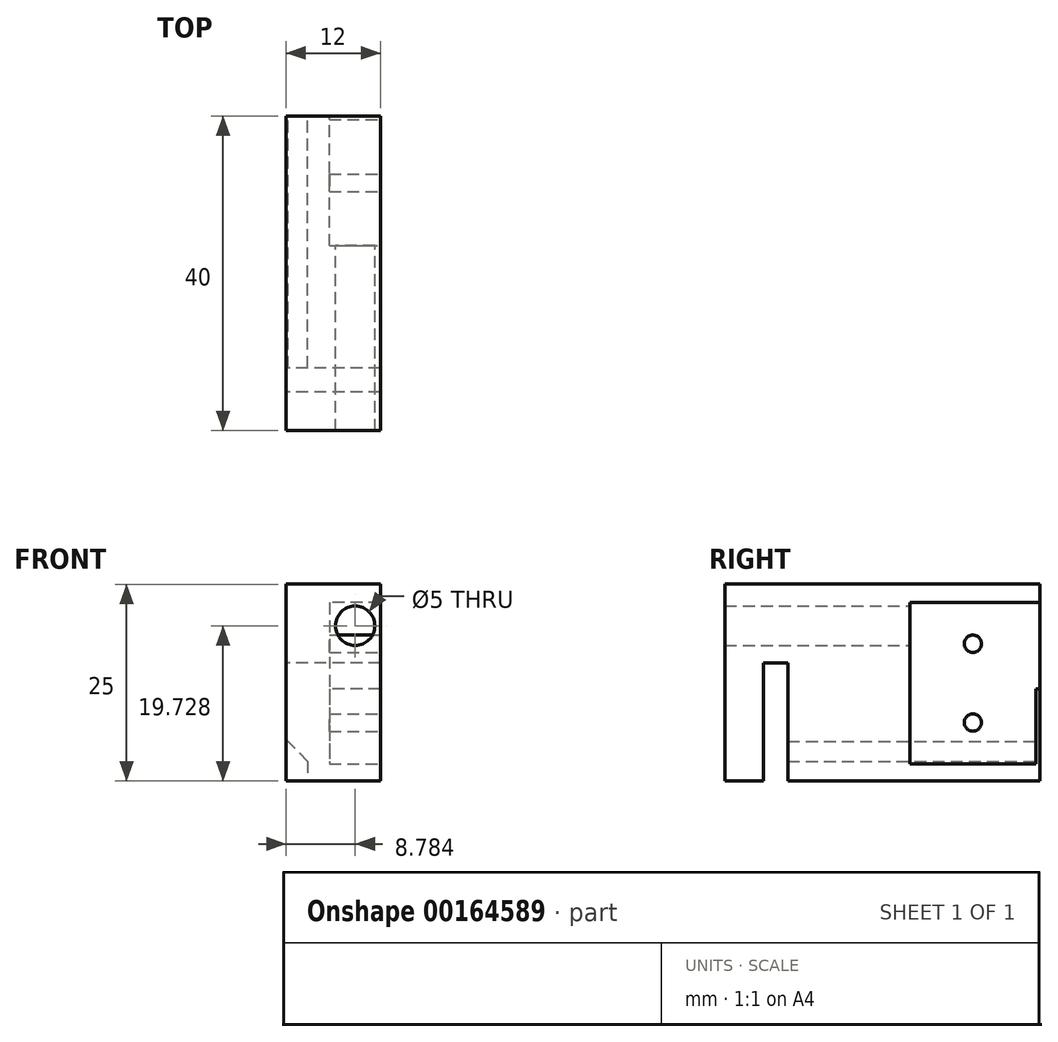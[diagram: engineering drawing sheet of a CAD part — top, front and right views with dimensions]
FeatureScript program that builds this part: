
annotation { "Feature Type Name" : "Feature", "Feature Type Description" : "" }
export const myFeature = defineFeature(function(context is Context, id is Id, definition is map)
    precondition{}
    {
        {
            var Q0;
            Q0=qCreatedBy(makeId("Right.planeOp"),FACE);
            var sketch = newSketch(context, id + "F0", { "sketchPlane" : qUnion([Q0])});
            skLineSegment(sketch, "E0.bottom", {"start": v(-4.9, -0.08) * mm, "end": v(35.1, -0.08) * mm});
            skLineSegment(sketch, "E0.top", {"start": v(-4.9, -25.08) * mm, "end": v(35.1, -25.08) * mm});
            skLineSegment(sketch, "E0.left", {"start": v(-4.9, -0.08) * mm, "end": v(-4.9, -25.08) * mm});
            skLineSegment(sketch, "E0.right", {"start": v(35.1, -0.08) * mm, "end": v(35.1, -25.08) * mm});
            skLineSegment(sketch, "E1.bottom", {"start": v(0, -25.08) * mm, "end": v(3.1, -25.08) * mm});
            skLineSegment(sketch, "E1.top", {"start": v(0, -10.08) * mm, "end": v(3.1, -10.08) * mm});
            skLineSegment(sketch, "E1.left", {"start": v(0, -25.08) * mm, "end": v(0, -10.08) * mm});
            skLineSegment(sketch, "E1.right", {"start": v(3.1, -25.08) * mm, "end": v(3.1, -10.08) * mm});
            skSolve(sketch);
        }
        {
            var Q0;
            Q0=makeQuery(id+"F0.imprint","IMPRINT",FACE,{"disambiguationData":[TD([[makeQuery(id+"F0.imprint","IMPRINT",EDGE,{"derivedFrom":sQuery(id+"F0.wireOp",EDGE,"E0.bottom")}),-1.0]])]});
            extrude(context, id + "F1", {"entities" : qUnion([Q0]), "depth" : 12 * mm});
        }
        {
            var Q0;
            Q0=makeQuery(id+"F1.opExtrude","CAP_FACE",FACE,{"disambiguationData":[OSD([sQuery(id+"F0.wireOp",EDGE,"E0.bottom"),sQuery(id+"F0.wireOp",EDGE,"E0.top"),sQuery(id+"F0.wireOp",EDGE,"E0.left"),sQuery(id+"F0.wireOp",EDGE,"E0.right"),sQuery(id+"F0.wireOp",EDGE,"E1.top"),sQuery(id+"F0.wireOp",EDGE,"E1.left"),sQuery(id+"F0.wireOp",EDGE,"E1.right")])],"isStart":false});
            var sketch = newSketch(context, id + "F2", { "sketchPlane" : qUnion([Q0])});
            skLineSegment(sketch, "E2.bottom", {"start": v(18.6, -2.4) * mm, "end": v(34.6, -2.4) * mm});
            skLineSegment(sketch, "E2.top", {"start": v(18.6, -22.9) * mm, "end": v(34.6, -22.9) * mm});
            skLineSegment(sketch, "E2.left", {"start": v(18.6, -2.4) * mm, "end": v(18.6, -22.9) * mm});
            skLineSegment(sketch, "E2.right", {"start": v(34.6, -13.4) * mm, "end": v(34.6, -22.9) * mm});
            skLineSegment(sketch, "E3.bottom", {"start": v(34.6, -2.4) * mm, "end": v(38.48, -2.4) * mm});
            skLineSegment(sketch, "E3.top", {"start": v(34.6, -13.4) * mm, "end": v(38.48, -13.4) * mm});
            skLineSegment(sketch, "E3.right", {"start": v(38.48, -2.4) * mm, "end": v(38.48, -13.4) * mm});
            skCircle(sketch, "E4", {"center": v(26.6, -7.65) * mm, "radius": 1.1 * mm});
            skCircle(sketch, "E5", {"center": v(26.6, -17.65) * mm, "radius": 1.1 * mm});
            skSolve(sketch);
        }
        {
            var Q0;
            Q0 = qSketchRegion(id + "F2", true);
            extrude(context, id + "F3", {"entities" : qUnion([Q0]), "operationType" : NewBodyOperationType.REMOVE, "oppositeDirection" : true, "depth" : 6.5 * mm});
        }
        {
            var Q0;
            Q0=makeQuery(id+"F3.boolean.opBoolean","COPY",FACE,{"derivedFrom":makeQuery(id+"F3.opExtrude","SWEPT_FACE",FACE,{"disambiguationData":[OSD([sQuery(id+"F2.wireOp",EDGE,"E2.left")])]})});
            var sketch = newSketch(context, id + "F4", { "sketchPlane" : qUnion([Q0])});
            skCircle(sketch, "E6", {"center": v(-8.78, -5.35) * mm, "radius": 2.5 * mm});
            skSolve(sketch);
        }
        {
            var Q0;
            Q0 = qSketchRegion(id + "F4", true);
            extrude(context, id + "F5", {"entities" : qUnion([Q0]), "operationType" : NewBodyOperationType.REMOVE, "oppositeDirection" : true, "depth" : 25 * mm});
        }
        {
            var Q0;
            Q0=makeQuery(id+"F1.opExtrude","SWEPT_FACE",FACE,{"disambiguationData":[OSD([sQuery(id+"F0.wireOp",EDGE,"E0.right")])]});
            var sketch = newSketch(context, id + "F6", { "sketchPlane" : qUnion([Q0])});
            skLineSegment(sketch, "E7.bottom", {"start": v(-2.75, -20.08) * mm, "end": v(1.34, -20.08) * mm});
            skLineSegment(sketch, "E7.top", {"start": v(-2.75, -25.08) * mm, "end": v(1.34, -25.08) * mm});
            skLineSegment(sketch, "E7.left", {"start": v(-2.75, -20.08) * mm, "end": v(-2.75, -25.08) * mm});
            skLineSegment(sketch, "E7.right", {"start": v(1.34, -20.08) * mm, "end": v(1.34, -25.08) * mm});
            skLineSegment(sketch, "E8", {"start": v(-2.75, -22.58) * mm, "end": v(-0.25, -20.08) * mm});
            skLineSegment(sketch, "E9", {"start": v(-0.25, -20.08) * mm, "end": v(0, -20.33) * mm});
            skPoint(sketch, "E10.0", {"position": v(-12, -10.08) * mm});
            skSolve(sketch);
        }
        {
            var Q0;
            {var subQ0=sQuery(id+"F6.wireOp",EDGE,"E9");Q0=makeQuery(id+"F6.imprint","IMPRINT",FACE,{"disambiguationData":[TD([[makeQuery(id+"F6.imprint","IMPRINT",EDGE,{"derivedFrom":subQ0}),1.0]])]});}
            var Q1;
            {var subQ1=sQuery(id+"F6.wireOp",EDGE,"E8");Q1=makeQuery(id+"F6.imprint","IMPRINT",FACE,{"disambiguationData":[TD([[makeQuery(id+"F6.imprint","IMPRINT",EDGE,{"derivedFrom":subQ1}),-1.0]])]});}
            var Q2;
            {var subQ0=sQuery(id+"F6.wireOp",EDGE,"E7.right");Q2=makeQuery(id+"F6.imprint","IMPRINT",FACE,{"disambiguationData":[TD([[makeQuery(id+"F6.imprint","IMPRINT",EDGE,{"derivedFrom":subQ0}),-1.0]])]});}
            var Q3;
            Q3=makeQuery(id+"F1.opExtrude","SWEPT_FACE",FACE,{"disambiguationData":[OSD([sQuery(id+"F0.wireOp",EDGE,"E1.right")])]});
            extrude(context, id + "F7", {"entities" : qUnion([Q0, Q1, Q2]), "operationType" : NewBodyOperationType.REMOVE, "endBound" : BoundingType.UP_TO_SURFACE, "oppositeDirection" : true, "endBoundEntityFace" : qUnion([Q3]), "depth" : 25 * mm});
        }
    });
